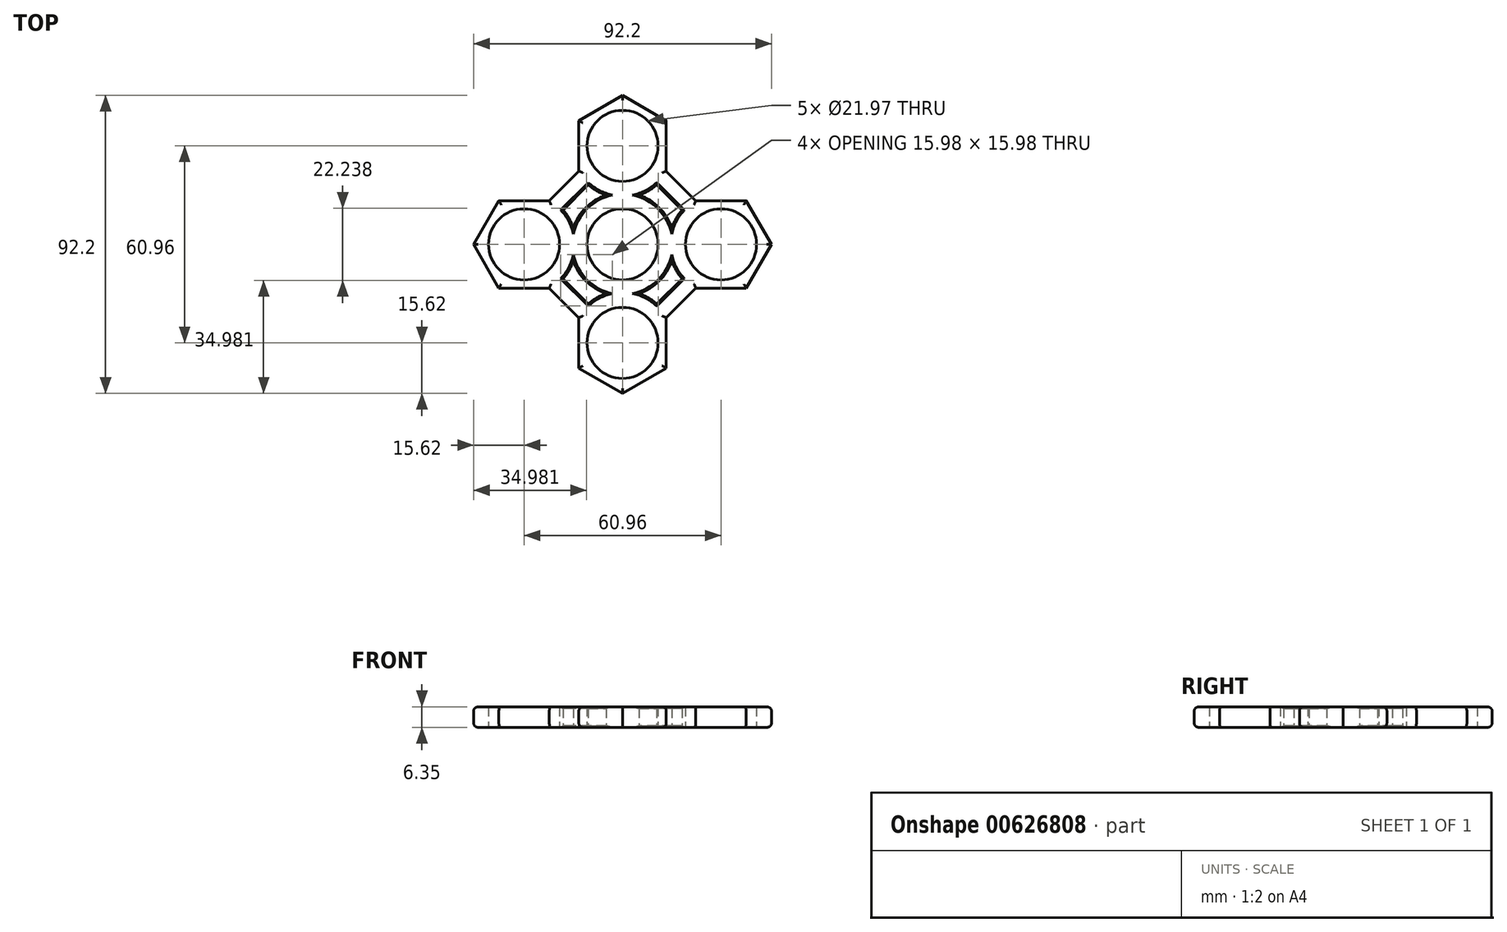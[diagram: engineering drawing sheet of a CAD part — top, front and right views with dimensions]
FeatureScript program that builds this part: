
annotation { "Feature Type Name" : "Feature", "Feature Type Description" : "" }
export const myFeature = defineFeature(function(context is Context, id is Id, definition is map)
    precondition{}
    {
        {
            var Q0;
            Q0=qCreatedBy(makeId("Top.planeOp"),FACE);
            var sketch = newSketch(context, id + "F0", { "sketchPlane" : qUnion([Q0])});
            skCircle(sketch, "E0", {"center": v(0, 0) * mm, "radius": 10.99 * mm});
            skCircle(sketch, "E1", {"center": v(0, 0) * mm, "radius": 13.53 * mm});
            skLineSegment(sketch, "E2", {"start": v(0, 0) * mm, "end": v(0, 30.48) * mm});
            skLineSegment(sketch, "E3", {"start": v(0, 0) * mm, "end": v(0, -30.48) * mm});
            skLineSegment(sketch, "E4", {"start": v(0, 0) * mm, "end": v(30.48, 0) * mm});
            skLineSegment(sketch, "E5", {"start": v(0, 0) * mm, "end": v(-30.48, 0) * mm});
            skCircle(sketch, "E6", {"center": v(0, 30.48) * mm, "radius": 13.53 * mm});
            skCircle(sketch, "E7", {"center": v(0, 30.48) * mm, "radius": 10.99 * mm});
            skCircle(sketch, "E8", {"center": v(30.48, 0) * mm, "radius": 13.53 * mm});
            skCircle(sketch, "E9", {"center": v(30.48, 0) * mm, "radius": 10.99 * mm});
            skCircle(sketch, "E10", {"center": v(0, -30.48) * mm, "radius": 13.53 * mm});
            skCircle(sketch, "E11", {"center": v(0, -30.48) * mm, "radius": 10.99 * mm});
            skCircle(sketch, "E12", {"center": v(-30.48, 0) * mm, "radius": 13.53 * mm});
            skCircle(sketch, "E13", {"center": v(-30.48, 0) * mm, "radius": 10.99 * mm});
            skCircle(sketch, "E14.cCircle", {"center": v(0, 0) * mm, "radius": 13.53 * mm, "construction": true});
            skLineSegment(sketch, "E14.0", {"start": v(13.53, 7.8) * mm, "end": v(13.53, -7.8) * mm});
            skLineSegment(sketch, "E14.1", {"start": v(13.53, -7.8) * mm, "end": v(0, -15.62) * mm});
            skLineSegment(sketch, "E14.2", {"start": v(0, -15.62) * mm, "end": v(-13.53, -7.8) * mm});
            skLineSegment(sketch, "E14.3", {"start": v(-13.53, -7.8) * mm, "end": v(-13.53, 7.8) * mm});
            skLineSegment(sketch, "E14.4", {"start": v(-13.53, 7.8) * mm, "end": v(0, 15.62) * mm});
            skLineSegment(sketch, "E14.5", {"start": v(0, 15.62) * mm, "end": v(13.53, 7.8) * mm});
            skPoint(sketch, "E14.0.midPoint", {"position": v(13.53, 0) * mm});
            skCircle(sketch, "E15.cCircle", {"center": v(0, 30.48) * mm, "radius": 13.53 * mm, "construction": true});
            skLineSegment(sketch, "E15.0", {"start": v(13.53, 38.29) * mm, "end": v(13.53, 22.67) * mm});
            skLineSegment(sketch, "E15.1", {"start": v(13.53, 22.67) * mm, "end": v(0, 14.86) * mm});
            skLineSegment(sketch, "E15.2", {"start": v(0, 14.86) * mm, "end": v(-13.53, 22.67) * mm});
            skLineSegment(sketch, "E15.3", {"start": v(-13.53, 22.67) * mm, "end": v(-13.53, 38.29) * mm});
            skLineSegment(sketch, "E15.4", {"start": v(-13.53, 38.29) * mm, "end": v(0, 46.1) * mm});
            skLineSegment(sketch, "E15.5", {"start": v(0, 46.1) * mm, "end": v(13.53, 38.29) * mm});
            skPoint(sketch, "E15.0.midPoint", {"position": v(13.53, 30.48) * mm});
            skCircle(sketch, "E16.cCircle", {"center": v(0, -30.48) * mm, "radius": 13.53 * mm, "construction": true});
            skLineSegment(sketch, "E16.0", {"start": v(13.53, -22.67) * mm, "end": v(13.53, -38.29) * mm});
            skLineSegment(sketch, "E16.1", {"start": v(13.53, -38.29) * mm, "end": v(0, -46.1) * mm});
            skLineSegment(sketch, "E16.2", {"start": v(0, -46.1) * mm, "end": v(-13.53, -38.29) * mm});
            skLineSegment(sketch, "E16.3", {"start": v(-13.53, -38.29) * mm, "end": v(-13.53, -22.67) * mm});
            skLineSegment(sketch, "E16.4", {"start": v(-13.53, -22.67) * mm, "end": v(0, -14.86) * mm});
            skLineSegment(sketch, "E16.5", {"start": v(0, -14.86) * mm, "end": v(13.53, -22.67) * mm});
            skPoint(sketch, "E16.0.midPoint", {"position": v(13.53, -30.48) * mm});
            skCircle(sketch, "E17.cCircle", {"center": v(30.48, 0) * mm, "radius": 13.53 * mm, "construction": true});
            skLineSegment(sketch, "E17.0", {"start": v(22.67, 13.53) * mm, "end": v(38.29, 13.53) * mm});
            skLineSegment(sketch, "E17.1", {"start": v(38.29, 13.53) * mm, "end": v(46.1, 0) * mm});
            skLineSegment(sketch, "E17.2", {"start": v(46.1, 0) * mm, "end": v(38.29, -13.53) * mm});
            skLineSegment(sketch, "E17.3", {"start": v(38.29, -13.53) * mm, "end": v(22.67, -13.53) * mm});
            skLineSegment(sketch, "E17.4", {"start": v(22.67, -13.53) * mm, "end": v(14.86, 0) * mm});
            skLineSegment(sketch, "E17.5", {"start": v(14.86, 0) * mm, "end": v(22.67, 13.53) * mm});
            skPoint(sketch, "E17.0.midPoint", {"position": v(30.48, 13.53) * mm});
            skCircle(sketch, "E18.cCircle", {"center": v(-30.48, 0) * mm, "radius": 13.53 * mm, "construction": true});
            skLineSegment(sketch, "E18.0", {"start": v(-22.67, -13.53) * mm, "end": v(-38.29, -13.53) * mm});
            skLineSegment(sketch, "E18.1", {"start": v(-38.29, -13.53) * mm, "end": v(-46.1, 0) * mm});
            skLineSegment(sketch, "E18.2", {"start": v(-46.1, 0) * mm, "end": v(-38.29, 13.53) * mm});
            skLineSegment(sketch, "E18.3", {"start": v(-38.29, 13.53) * mm, "end": v(-22.67, 13.53) * mm});
            skLineSegment(sketch, "E18.4", {"start": v(-22.67, 13.53) * mm, "end": v(-14.86, 0) * mm});
            skLineSegment(sketch, "E18.5", {"start": v(-14.86, 0) * mm, "end": v(-22.67, -13.53) * mm});
            skPoint(sketch, "E18.0.midPoint", {"position": v(-30.48, -13.53) * mm});
            skLineSegment(sketch, "E19", {"start": v(-22.67, 13.53) * mm, "end": v(-13.53, 22.67) * mm});
            skLineSegment(sketch, "E20", {"start": v(-22.67, -13.53) * mm, "end": v(-13.53, -22.67) * mm});
            skLineSegment(sketch, "E21", {"start": v(13.53, -22.67) * mm, "end": v(22.67, -13.53) * mm});
            skLineSegment(sketch, "E22", {"start": v(22.67, 13.53) * mm, "end": v(13.53, 22.67) * mm});
            skSolve(sketch);
        }
        {
            var Q0;
            {var subQ0=sQuery(id+"F0.wireOp",EDGE,"E14.5");var subQ3=sQuery(id+"F0.wireOp",EDGE,"E14.0");var subQ5=makeQuery(id+"F0.imprint","INTERSECT",VERTEX,{"derivedFrom":[subQ3,subQ0]});Q0=makeQuery(id+"F0.imprint","IMPRINT",FACE,{"disambiguationData":[TD([[makeQuery(id+"F0.imprint","IMPRINT",EDGE,{"disambiguationData":[TD([[subQ5,1.0]])],"derivedFrom":subQ0}),-1.0]])]});}
            var Q1;
            {var subQ0=sQuery(id+"F0.wireOp",EDGE,"E14.4");var subQ3=sQuery(id+"F0.wireOp",EDGE,"E14.3");var subQ5=makeQuery(id+"F0.imprint","INTERSECT",VERTEX,{"derivedFrom":[subQ3,subQ0]});Q1=makeQuery(id+"F0.imprint","IMPRINT",FACE,{"disambiguationData":[TD([[makeQuery(id+"F0.imprint","IMPRINT",EDGE,{"disambiguationData":[TD([[subQ5,-1.0]])],"derivedFrom":subQ0}),-1.0]])]});}
            var Q2;
            {var subQ0=sQuery(id+"F0.wireOp",EDGE,"E14.2");var subQ3=sQuery(id+"F0.wireOp",EDGE,"E14.3");var subQ5=makeQuery(id+"F0.imprint","INTERSECT",VERTEX,{"derivedFrom":[subQ0,subQ3]});Q2=makeQuery(id+"F0.imprint","IMPRINT",FACE,{"disambiguationData":[TD([[makeQuery(id+"F0.imprint","IMPRINT",EDGE,{"disambiguationData":[TD([[subQ5,1.0]])],"derivedFrom":subQ0}),-1.0]])]});}
            var Q3;
            {var subQ0=sQuery(id+"F0.wireOp",EDGE,"E14.1");var subQ3=sQuery(id+"F0.wireOp",EDGE,"E14.0");var subQ5=makeQuery(id+"F0.imprint","INTERSECT",VERTEX,{"derivedFrom":[subQ3,subQ0]});Q3=makeQuery(id+"F0.imprint","IMPRINT",FACE,{"disambiguationData":[TD([[makeQuery(id+"F0.imprint","IMPRINT",EDGE,{"disambiguationData":[TD([[subQ5,-1.0]])],"derivedFrom":subQ0}),-1.0]])]});}
            var Q4;
            {var subQ0=sQuery(id+"F0.wireOp",EDGE,"E15.5");var subQ1=sQuery(id+"F0.wireOp",EDGE,"E6");var subQ2=makeQuery(id+"F0.imprint","INTERSECT",VERTEX,{"derivedFrom":[subQ1,subQ0]});Q4=makeQuery(id+"F0.imprint","IMPRINT",FACE,{"disambiguationData":[TD([[makeQuery(id+"F0.imprint","IMPRINT",EDGE,{"disambiguationData":[TD([[subQ2,1.0]])],"derivedFrom":subQ1}),-1.0]])]});}
            var Q5;
            {var subQ0=sQuery(id+"F0.wireOp",EDGE,"E15.5");var subQ1=sQuery(id+"F0.wireOp",EDGE,"E6");var subQ2=makeQuery(id+"F0.imprint","INTERSECT",VERTEX,{"derivedFrom":[subQ1,subQ0]});Q5=makeQuery(id+"F0.imprint","IMPRINT",FACE,{"disambiguationData":[TD([[makeQuery(id+"F0.imprint","IMPRINT",EDGE,{"disambiguationData":[TD([[subQ2,-1.0]])],"derivedFrom":subQ1}),-1.0]])]});}
            var Q6;
            {var subQ0=sQuery(id+"F0.wireOp",EDGE,"E15.4");var subQ1=sQuery(id+"F0.wireOp",EDGE,"E6");var subQ2=makeQuery(id+"F0.imprint","INTERSECT",VERTEX,{"derivedFrom":[subQ1,subQ0]});Q6=makeQuery(id+"F0.imprint","IMPRINT",FACE,{"disambiguationData":[TD([[makeQuery(id+"F0.imprint","IMPRINT",EDGE,{"disambiguationData":[TD([[subQ2,-1.0]])],"derivedFrom":subQ1}),-1.0]])]});}
            var Q7;
            {var subQ0=sQuery(id+"F0.wireOp",EDGE,"E15.3");var subQ1=sQuery(id+"F0.wireOp",EDGE,"E6");var subQ2=makeQuery(id+"F0.imprint","INTERSECT",VERTEX,{"derivedFrom":[subQ1,subQ0]});Q7=makeQuery(id+"F0.imprint","IMPRINT",FACE,{"disambiguationData":[TD([[makeQuery(id+"F0.imprint","IMPRINT",EDGE,{"disambiguationData":[TD([[subQ2,-1.0]])],"derivedFrom":subQ1}),-1.0]])]});}
            var Q8;
            {var subQ0=sQuery(id+"F0.wireOp",EDGE,"E15.0");var subQ1=sQuery(id+"F0.wireOp",EDGE,"E6");var subQ2=makeQuery(id+"F0.imprint","INTERSECT",VERTEX,{"derivedFrom":[subQ1,subQ0]});Q8=makeQuery(id+"F0.imprint","IMPRINT",FACE,{"disambiguationData":[TD([[makeQuery(id+"F0.imprint","IMPRINT",EDGE,{"disambiguationData":[TD([[subQ2,1.0]])],"derivedFrom":subQ1}),-1.0]])]});}
            var Q9;
            {var subQ0=sQuery(id+"F0.wireOp",EDGE,"E17.0");var subQ1=sQuery(id+"F0.wireOp",EDGE,"E8");var subQ2=makeQuery(id+"F0.imprint","INTERSECT",VERTEX,{"derivedFrom":[subQ1,subQ0]});Q9=makeQuery(id+"F0.imprint","IMPRINT",FACE,{"disambiguationData":[TD([[makeQuery(id+"F0.imprint","IMPRINT",EDGE,{"disambiguationData":[TD([[subQ2,1.0]])],"derivedFrom":subQ1}),-1.0]])]});}
            var Q10;
            {var subQ0=sQuery(id+"F0.wireOp",EDGE,"E17.0");var subQ1=sQuery(id+"F0.wireOp",EDGE,"E8");var subQ2=makeQuery(id+"F0.imprint","INTERSECT",VERTEX,{"derivedFrom":[subQ1,subQ0]});Q10=makeQuery(id+"F0.imprint","IMPRINT",FACE,{"disambiguationData":[TD([[makeQuery(id+"F0.imprint","IMPRINT",EDGE,{"disambiguationData":[TD([[subQ2,-1.0]])],"derivedFrom":subQ1}),-1.0]])]});}
            var Q11;
            {var subQ0=sQuery(id+"F0.wireOp",EDGE,"E17.4");var subQ1=sQuery(id+"F0.wireOp",EDGE,"E8");var subQ2=makeQuery(id+"F0.imprint","INTERSECT",VERTEX,{"derivedFrom":[subQ1,subQ0]});Q11=makeQuery(id+"F0.imprint","IMPRINT",FACE,{"disambiguationData":[TD([[makeQuery(id+"F0.imprint","IMPRINT",EDGE,{"disambiguationData":[TD([[subQ2,-1.0]])],"derivedFrom":subQ1}),-1.0]])]});}
            var Q12;
            {var subQ0=sQuery(id+"F0.wireOp",EDGE,"E17.3");var subQ1=sQuery(id+"F0.wireOp",EDGE,"E8");var subQ2=makeQuery(id+"F0.imprint","INTERSECT",VERTEX,{"derivedFrom":[subQ1,subQ0]});Q12=makeQuery(id+"F0.imprint","IMPRINT",FACE,{"disambiguationData":[TD([[makeQuery(id+"F0.imprint","IMPRINT",EDGE,{"disambiguationData":[TD([[subQ2,-1.0]])],"derivedFrom":subQ1}),-1.0]])]});}
            var Q13;
            {var subQ0=sQuery(id+"F0.wireOp",EDGE,"E17.1");var subQ1=sQuery(id+"F0.wireOp",EDGE,"E8");var subQ2=makeQuery(id+"F0.imprint","INTERSECT",VERTEX,{"derivedFrom":[subQ1,subQ0]});Q13=makeQuery(id+"F0.imprint","IMPRINT",FACE,{"disambiguationData":[TD([[makeQuery(id+"F0.imprint","IMPRINT",EDGE,{"disambiguationData":[TD([[subQ2,1.0]])],"derivedFrom":subQ1}),-1.0]])]});}
            var Q14;
            {var subQ0=sQuery(id+"F0.wireOp",EDGE,"E16.5");var subQ1=sQuery(id+"F0.wireOp",EDGE,"E10");var subQ2=makeQuery(id+"F0.imprint","INTERSECT",VERTEX,{"derivedFrom":[subQ1,subQ0]});Q14=makeQuery(id+"F0.imprint","IMPRINT",FACE,{"disambiguationData":[TD([[makeQuery(id+"F0.imprint","IMPRINT",EDGE,{"disambiguationData":[TD([[subQ2,1.0]])],"derivedFrom":subQ1}),-1.0]])]});}
            var Q15;
            {var subQ0=sQuery(id+"F0.wireOp",EDGE,"E16.4");var subQ1=sQuery(id+"F0.wireOp",EDGE,"E10");var subQ2=makeQuery(id+"F0.imprint","INTERSECT",VERTEX,{"derivedFrom":[subQ1,subQ0]});Q15=makeQuery(id+"F0.imprint","IMPRINT",FACE,{"disambiguationData":[TD([[makeQuery(id+"F0.imprint","IMPRINT",EDGE,{"disambiguationData":[TD([[subQ2,-1.0]])],"derivedFrom":subQ1}),-1.0]])]});}
            var Q16;
            {var subQ0=sQuery(id+"F0.wireOp",EDGE,"E16.3");var subQ1=sQuery(id+"F0.wireOp",EDGE,"E10");var subQ2=makeQuery(id+"F0.imprint","INTERSECT",VERTEX,{"derivedFrom":[subQ1,subQ0]});Q16=makeQuery(id+"F0.imprint","IMPRINT",FACE,{"disambiguationData":[TD([[makeQuery(id+"F0.imprint","IMPRINT",EDGE,{"disambiguationData":[TD([[subQ2,-1.0]])],"derivedFrom":subQ1}),-1.0]])]});}
            var Q17;
            {var subQ0=sQuery(id+"F0.wireOp",EDGE,"E16.2");var subQ1=sQuery(id+"F0.wireOp",EDGE,"E10");var subQ2=makeQuery(id+"F0.imprint","INTERSECT",VERTEX,{"derivedFrom":[subQ1,subQ0]});Q17=makeQuery(id+"F0.imprint","IMPRINT",FACE,{"disambiguationData":[TD([[makeQuery(id+"F0.imprint","IMPRINT",EDGE,{"disambiguationData":[TD([[subQ2,-1.0]])],"derivedFrom":subQ1}),-1.0]])]});}
            var Q18;
            {var subQ0=sQuery(id+"F0.wireOp",EDGE,"E16.0");var subQ1=sQuery(id+"F0.wireOp",EDGE,"E10");var subQ2=makeQuery(id+"F0.imprint","INTERSECT",VERTEX,{"derivedFrom":[subQ1,subQ0]});Q18=makeQuery(id+"F0.imprint","IMPRINT",FACE,{"disambiguationData":[TD([[makeQuery(id+"F0.imprint","IMPRINT",EDGE,{"disambiguationData":[TD([[subQ2,1.0]])],"derivedFrom":subQ1}),-1.0]])]});}
            var Q19;
            {var subQ0=sQuery(id+"F0.wireOp",EDGE,"E18.4");var subQ1=sQuery(id+"F0.wireOp",EDGE,"E12");var subQ2=makeQuery(id+"F0.imprint","INTERSECT",VERTEX,{"derivedFrom":[subQ1,subQ0]});Q19=makeQuery(id+"F0.imprint","IMPRINT",FACE,{"disambiguationData":[TD([[makeQuery(id+"F0.imprint","IMPRINT",EDGE,{"disambiguationData":[TD([[subQ2,-1.0]])],"derivedFrom":subQ1}),-1.0]])]});}
            var Q20;
            {var subQ0=sQuery(id+"F0.wireOp",EDGE,"E18.3");var subQ1=sQuery(id+"F0.wireOp",EDGE,"E12");var subQ2=makeQuery(id+"F0.imprint","INTERSECT",VERTEX,{"derivedFrom":[subQ1,subQ0]});Q20=makeQuery(id+"F0.imprint","IMPRINT",FACE,{"disambiguationData":[TD([[makeQuery(id+"F0.imprint","IMPRINT",EDGE,{"disambiguationData":[TD([[subQ2,-1.0]])],"derivedFrom":subQ1}),-1.0]])]});}
            var Q21;
            {var subQ0=sQuery(id+"F0.wireOp",EDGE,"E18.2");var subQ1=sQuery(id+"F0.wireOp",EDGE,"E12");var subQ2=makeQuery(id+"F0.imprint","INTERSECT",VERTEX,{"derivedFrom":[subQ1,subQ0]});Q21=makeQuery(id+"F0.imprint","IMPRINT",FACE,{"disambiguationData":[TD([[makeQuery(id+"F0.imprint","IMPRINT",EDGE,{"disambiguationData":[TD([[subQ2,-1.0]])],"derivedFrom":subQ1}),-1.0]])]});}
            var Q22;
            {var subQ0=sQuery(id+"F0.wireOp",EDGE,"E18.1");var subQ1=sQuery(id+"F0.wireOp",EDGE,"E12");var subQ2=makeQuery(id+"F0.imprint","INTERSECT",VERTEX,{"derivedFrom":[subQ1,subQ0]});Q22=makeQuery(id+"F0.imprint","IMPRINT",FACE,{"disambiguationData":[TD([[makeQuery(id+"F0.imprint","IMPRINT",EDGE,{"disambiguationData":[TD([[subQ2,-1.0]])],"derivedFrom":subQ1}),-1.0]])]});}
            var Q23;
            {var subQ0=sQuery(id+"F0.wireOp",EDGE,"E18.0");var subQ1=sQuery(id+"F0.wireOp",EDGE,"E12");var subQ2=makeQuery(id+"F0.imprint","INTERSECT",VERTEX,{"derivedFrom":[subQ1,subQ0]});Q23=makeQuery(id+"F0.imprint","IMPRINT",FACE,{"disambiguationData":[TD([[makeQuery(id+"F0.imprint","IMPRINT",EDGE,{"disambiguationData":[TD([[subQ2,-1.0]])],"derivedFrom":subQ1}),-1.0]])]});}
            var Q24;
            {var subQ1=sQuery(id+"F0.wireOp",EDGE,"E4");var subQ3=sQuery(id+"F0.wireOp",EDGE,"E8");var subQ4=makeQuery(id+"F0.imprint","INTERSECT",VERTEX,{"derivedFrom":[subQ1,subQ3]});Q24=makeQuery(id+"F0.imprint","IMPRINT",FACE,{"disambiguationData":[TD([[makeQuery(id+"F0.imprint","IMPRINT",EDGE,{"disambiguationData":[TD([[subQ4,1.0]])],"derivedFrom":subQ3}),-1.0]])]});}
            var Q25;
            {var subQ1=sQuery(id+"F0.wireOp",EDGE,"E4");var subQ3=sQuery(id+"F0.wireOp",EDGE,"E8");var subQ4=makeQuery(id+"F0.imprint","INTERSECT",VERTEX,{"derivedFrom":[subQ1,subQ3]});Q25=makeQuery(id+"F0.imprint","IMPRINT",FACE,{"disambiguationData":[TD([[makeQuery(id+"F0.imprint","IMPRINT",EDGE,{"disambiguationData":[TD([[subQ4,-1.0]])],"derivedFrom":subQ3}),-1.0]])]});}
            var Q26;
            {var subQ1=sQuery(id+"F0.wireOp",EDGE,"E5");var subQ3=sQuery(id+"F0.wireOp",EDGE,"E12");var subQ4=makeQuery(id+"F0.imprint","INTERSECT",VERTEX,{"derivedFrom":[subQ1,subQ3]});Q26=makeQuery(id+"F0.imprint","IMPRINT",FACE,{"disambiguationData":[TD([[makeQuery(id+"F0.imprint","IMPRINT",EDGE,{"disambiguationData":[TD([[subQ4,-1.0]])],"derivedFrom":subQ3}),-1.0]])]});}
            var Q27;
            {var subQ1=sQuery(id+"F0.wireOp",EDGE,"E5");var subQ3=sQuery(id+"F0.wireOp",EDGE,"E12");var subQ4=makeQuery(id+"F0.imprint","INTERSECT",VERTEX,{"derivedFrom":[subQ1,subQ3]});Q27=makeQuery(id+"F0.imprint","IMPRINT",FACE,{"disambiguationData":[TD([[makeQuery(id+"F0.imprint","IMPRINT",EDGE,{"disambiguationData":[TD([[subQ4,1.0]])],"derivedFrom":subQ3}),-1.0]])]});}
            var Q28;
            {var subQ0=sQuery(id+"F0.wireOp",EDGE,"E14.5");var subQ1=sQuery(id+"F0.wireOp",EDGE,"E1");var subQ2=makeQuery(id+"F0.imprint","INTERSECT",VERTEX,{"derivedFrom":[subQ1,subQ0]});Q28=makeQuery(id+"F0.imprint","IMPRINT",FACE,{"disambiguationData":[TD([[makeQuery(id+"F0.imprint","IMPRINT",EDGE,{"disambiguationData":[TD([[subQ2,-1.0]])],"derivedFrom":subQ1}),-1.0]])]});}
            var Q29;
            {var subQ0=sQuery(id+"F0.wireOp",EDGE,"E14.4");var subQ1=sQuery(id+"F0.wireOp",EDGE,"E1");var subQ2=makeQuery(id+"F0.imprint","INTERSECT",VERTEX,{"derivedFrom":[subQ1,subQ0]});Q29=makeQuery(id+"F0.imprint","IMPRINT",FACE,{"disambiguationData":[TD([[makeQuery(id+"F0.imprint","IMPRINT",EDGE,{"disambiguationData":[TD([[subQ2,1.0]])],"derivedFrom":subQ1}),-1.0]])]});}
            var Q30;
            {var subQ0=sQuery(id+"F0.wireOp",EDGE,"E14.2");var subQ1=sQuery(id+"F0.wireOp",EDGE,"E1");var subQ2=makeQuery(id+"F0.imprint","INTERSECT",VERTEX,{"derivedFrom":[subQ1,subQ0]});Q30=makeQuery(id+"F0.imprint","IMPRINT",FACE,{"disambiguationData":[TD([[makeQuery(id+"F0.imprint","IMPRINT",EDGE,{"disambiguationData":[TD([[subQ2,-1.0]])],"derivedFrom":subQ1}),-1.0]])]});}
            var Q31;
            {var subQ0=sQuery(id+"F0.wireOp",EDGE,"E14.1");var subQ1=sQuery(id+"F0.wireOp",EDGE,"E1");var subQ2=makeQuery(id+"F0.imprint","INTERSECT",VERTEX,{"derivedFrom":[subQ1,subQ0]});Q31=makeQuery(id+"F0.imprint","IMPRINT",FACE,{"disambiguationData":[TD([[makeQuery(id+"F0.imprint","IMPRINT",EDGE,{"disambiguationData":[TD([[subQ2,1.0]])],"derivedFrom":subQ1}),-1.0]])]});}
            var Q32;
            {var subQ0=sQuery(id+"F0.wireOp",EDGE,"E14.4");var subQ3=sQuery(id+"F0.wireOp",EDGE,"E15.2");var subQ5=makeQuery(id+"F0.imprint","INTERSECT",VERTEX,{"derivedFrom":[subQ0,subQ3]});Q32=makeQuery(id+"F0.imprint","IMPRINT",FACE,{"disambiguationData":[TD([[makeQuery(id+"F0.imprint","IMPRINT",EDGE,{"disambiguationData":[TD([[subQ5,-1.0]])],"derivedFrom":subQ0}),-1.0]])]});}
            var Q33;
            {var subQ0=sQuery(id+"F0.wireOp",EDGE,"E14.5");var subQ3=sQuery(id+"F0.wireOp",EDGE,"E15.1");var subQ5=makeQuery(id+"F0.imprint","INTERSECT",VERTEX,{"derivedFrom":[subQ0,subQ3]});Q33=makeQuery(id+"F0.imprint","IMPRINT",FACE,{"disambiguationData":[TD([[makeQuery(id+"F0.imprint","IMPRINT",EDGE,{"disambiguationData":[TD([[subQ5,1.0]])],"derivedFrom":subQ0}),-1.0]])]});}
            var Q34;
            {var subQ1=sQuery(id+"F0.wireOp",EDGE,"E2");var subQ3=sQuery(id+"F0.wireOp",EDGE,"E6");var subQ4=makeQuery(id+"F0.imprint","INTERSECT",VERTEX,{"derivedFrom":[subQ1,subQ3]});Q34=makeQuery(id+"F0.imprint","IMPRINT",FACE,{"disambiguationData":[TD([[makeQuery(id+"F0.imprint","IMPRINT",EDGE,{"disambiguationData":[TD([[subQ4,1.0]])],"derivedFrom":subQ3}),-1.0]])]});}
            var Q35;
            {var subQ1=sQuery(id+"F0.wireOp",EDGE,"E2");var subQ3=sQuery(id+"F0.wireOp",EDGE,"E6");var subQ4=makeQuery(id+"F0.imprint","INTERSECT",VERTEX,{"derivedFrom":[subQ1,subQ3]});Q35=makeQuery(id+"F0.imprint","IMPRINT",FACE,{"disambiguationData":[TD([[makeQuery(id+"F0.imprint","IMPRINT",EDGE,{"disambiguationData":[TD([[subQ4,-1.0]])],"derivedFrom":subQ3}),-1.0]])]});}
            var Q36;
            {var subQ0=sQuery(id+"F0.wireOp",EDGE,"E14.1");var subQ3=sQuery(id+"F0.wireOp",EDGE,"E16.5");var subQ5=makeQuery(id+"F0.imprint","INTERSECT",VERTEX,{"derivedFrom":[subQ0,subQ3]});Q36=makeQuery(id+"F0.imprint","IMPRINT",FACE,{"disambiguationData":[TD([[makeQuery(id+"F0.imprint","IMPRINT",EDGE,{"disambiguationData":[TD([[subQ5,-1.0]])],"derivedFrom":subQ0}),-1.0]])]});}
            var Q37;
            {var subQ0=sQuery(id+"F0.wireOp",EDGE,"E14.2");var subQ3=sQuery(id+"F0.wireOp",EDGE,"E16.4");var subQ5=makeQuery(id+"F0.imprint","INTERSECT",VERTEX,{"derivedFrom":[subQ0,subQ3]});Q37=makeQuery(id+"F0.imprint","IMPRINT",FACE,{"disambiguationData":[TD([[makeQuery(id+"F0.imprint","IMPRINT",EDGE,{"disambiguationData":[TD([[subQ5,1.0]])],"derivedFrom":subQ0}),-1.0]])]});}
            var Q38;
            {var subQ1=sQuery(id+"F0.wireOp",EDGE,"E3");var subQ3=sQuery(id+"F0.wireOp",EDGE,"E10");var subQ4=makeQuery(id+"F0.imprint","INTERSECT",VERTEX,{"derivedFrom":[subQ1,subQ3]});Q38=makeQuery(id+"F0.imprint","IMPRINT",FACE,{"disambiguationData":[TD([[makeQuery(id+"F0.imprint","IMPRINT",EDGE,{"disambiguationData":[TD([[subQ4,1.0]])],"derivedFrom":subQ3}),-1.0]])]});}
            var Q39;
            {var subQ1=sQuery(id+"F0.wireOp",EDGE,"E3");var subQ3=sQuery(id+"F0.wireOp",EDGE,"E10");var subQ4=makeQuery(id+"F0.imprint","INTERSECT",VERTEX,{"derivedFrom":[subQ1,subQ3]});Q39=makeQuery(id+"F0.imprint","IMPRINT",FACE,{"disambiguationData":[TD([[makeQuery(id+"F0.imprint","IMPRINT",EDGE,{"disambiguationData":[TD([[subQ4,-1.0]])],"derivedFrom":subQ3}),-1.0]])]});}
            var Q40;
            {var subQ0=sQuery(id+"F0.wireOp",EDGE,"E2");var subQ1=sQuery(id+"F0.wireOp",EDGE,"E0");var subQ2=makeQuery(id+"F0.imprint","INTERSECT",VERTEX,{"derivedFrom":[subQ1,subQ0]});Q40=makeQuery(id+"F0.imprint","IMPRINT",FACE,{"disambiguationData":[TD([[makeQuery(id+"F0.imprint","IMPRINT",EDGE,{"disambiguationData":[TD([[subQ2,1.0]])],"derivedFrom":subQ1}),-1.0]])]});}
            var Q41;
            {var subQ0=sQuery(id+"F0.wireOp",EDGE,"E2");var subQ1=sQuery(id+"F0.wireOp",EDGE,"E0");var subQ2=makeQuery(id+"F0.imprint","INTERSECT",VERTEX,{"derivedFrom":[subQ1,subQ0]});Q41=makeQuery(id+"F0.imprint","IMPRINT",FACE,{"disambiguationData":[TD([[makeQuery(id+"F0.imprint","IMPRINT",EDGE,{"disambiguationData":[TD([[subQ2,-1.0]])],"derivedFrom":subQ1}),-1.0]])]});}
            var Q42;
            {var subQ4=sQuery(id+"F0.wireOp",EDGE,"E0");var subQ6=sQuery(id+"F0.wireOp",EDGE,"E5");var subQ8=makeQuery(id+"F0.imprint","INTERSECT",VERTEX,{"derivedFrom":[subQ4,subQ6]});Q42=makeQuery(id+"F0.imprint","IMPRINT",FACE,{"disambiguationData":[TD([[makeQuery(id+"F0.imprint","IMPRINT",EDGE,{"disambiguationData":[TD([[subQ8,-1.0]])],"derivedFrom":subQ4}),-1.0]])]});}
            var Q43;
            {var subQ2=sQuery(id+"F0.wireOp",EDGE,"E4");var subQ6=sQuery(id+"F0.wireOp",EDGE,"E0");var subQ8=makeQuery(id+"F0.imprint","INTERSECT",VERTEX,{"derivedFrom":[subQ6,subQ2]});Q43=makeQuery(id+"F0.imprint","IMPRINT",FACE,{"disambiguationData":[TD([[makeQuery(id+"F0.imprint","IMPRINT",EDGE,{"disambiguationData":[TD([[subQ8,1.0]])],"derivedFrom":subQ6}),-1.0]])]});}
            var Q44;
            Q44=makeQuery(id+"F0.imprint","IMPRINT",FACE,{"disambiguationData":[TD([[makeQuery(id+"F0.imprint","IMPRINT",EDGE,{"derivedFrom":sQuery(id+"F0.wireOp",EDGE,"E7")}),-1.0]])]});
            var Q45;
            Q45=makeQuery(id+"F0.imprint","IMPRINT",FACE,{"disambiguationData":[TD([[makeQuery(id+"F0.imprint","IMPRINT",EDGE,{"derivedFrom":sQuery(id+"F0.wireOp",EDGE,"E9")}),-1.0]])]});
            var Q46;
            Q46=makeQuery(id+"F0.imprint","IMPRINT",FACE,{"disambiguationData":[TD([[makeQuery(id+"F0.imprint","IMPRINT",EDGE,{"derivedFrom":sQuery(id+"F0.wireOp",EDGE,"E11")}),-1.0]])]});
            var Q47;
            Q47=makeQuery(id+"F0.imprint","IMPRINT",FACE,{"disambiguationData":[TD([[makeQuery(id+"F0.imprint","IMPRINT",EDGE,{"derivedFrom":sQuery(id+"F0.wireOp",EDGE,"E13")}),-1.0]])]});
            var Q48;
            {var subQ10=sQuery(id+"F0.wireOp",EDGE,"E19");Q48=makeQuery(id+"F0.imprint","IMPRINT",FACE,{"disambiguationData":[TD([[makeQuery(id+"F0.imprint","IMPRINT",EDGE,{"derivedFrom":subQ10}),-1.0]])]});}
            var Q49;
            {var subQ9=sQuery(id+"F0.wireOp",EDGE,"E22");Q49=makeQuery(id+"F0.imprint","IMPRINT",FACE,{"disambiguationData":[TD([[makeQuery(id+"F0.imprint","IMPRINT",EDGE,{"derivedFrom":subQ9}),1.0]])]});}
            var Q50;
            {var subQ13=sQuery(id+"F0.wireOp",EDGE,"E21");Q50=makeQuery(id+"F0.imprint","IMPRINT",FACE,{"disambiguationData":[TD([[makeQuery(id+"F0.imprint","IMPRINT",EDGE,{"derivedFrom":subQ13}),1.0]])]});}
            var Q51;
            {var subQ12=sQuery(id+"F0.wireOp",EDGE,"E20");Q51=makeQuery(id+"F0.imprint","IMPRINT",FACE,{"disambiguationData":[TD([[makeQuery(id+"F0.imprint","IMPRINT",EDGE,{"derivedFrom":subQ12}),1.0]])]});}
            extrude(context, id + "F1", {"entities" : qUnion([Q0, Q1, Q2, Q3, Q4, Q5, Q6, Q7, Q8, Q9, Q10, Q11, Q12, Q13, Q14, Q15, Q16, Q17, Q18, Q19, Q20, Q21, Q22, Q23, Q24, Q25, Q26, Q27, Q28, Q29, Q30, Q31, Q32, Q33, Q34, Q35, Q36, Q37, Q38, Q39, Q40, Q41, Q42, Q43, Q44, Q45, Q46, Q47, Q48, Q49, Q50, Q51]), "depth" : 6.35 * mm, "offsetDistance" : 25.4 * mm});
        }
        {
            var Q0;
            Q0=makeQuery(id+"F3.opFillet","SPLIT",FACE,{"disambiguationData":[OD(12.0)],"derivedFrom":makeQuery(id+"F1.opExtrude","CAP_FACE",FACE,{"disambiguationData":[OSD([sQuery(id+"F0.wireOp",EDGE,"E0"),sQuery(id+"F0.wireOp",EDGE,"E7"),sQuery(id+"F0.wireOp",EDGE,"E9"),sQuery(id+"F0.wireOp",EDGE,"E11"),sQuery(id+"F0.wireOp",EDGE,"E13"),sQuery(id+"F0.wireOp",EDGE,"E15.0"),sQuery(id+"F0.wireOp",EDGE,"E15.3"),sQuery(id+"F0.wireOp",EDGE,"E15.4"),sQuery(id+"F0.wireOp",EDGE,"E15.5"),sQuery(id+"F0.wireOp",EDGE,"E16.0"),sQuery(id+"F0.wireOp",EDGE,"E16.1"),sQuery(id+"F0.wireOp",EDGE,"E16.2"),sQuery(id+"F0.wireOp",EDGE,"E16.3"),sQuery(id+"F0.wireOp",EDGE,"E17.0"),sQuery(id+"F0.wireOp",EDGE,"E17.1"),sQuery(id+"F0.wireOp",EDGE,"E17.2"),sQuery(id+"F0.wireOp",EDGE,"E17.3"),sQuery(id+"F0.wireOp",EDGE,"E18.0"),sQuery(id+"F0.wireOp",EDGE,"E18.1"),sQuery(id+"F0.wireOp",EDGE,"E18.2"),sQuery(id+"F0.wireOp",EDGE,"E18.3"),sQuery(id+"F0.wireOp",EDGE,"E19"),sQuery(id+"F0.wireOp",EDGE,"E20"),sQuery(id+"F0.wireOp",EDGE,"E21"),sQuery(id+"F0.wireOp",EDGE,"E22")])],"isStart":false})});
            var Q1;
            Q1=makeQuery(id+"F1.opExtrude","CAP_FACE",FACE,{"disambiguationData":[OSD([sQuery(id+"F0.wireOp",EDGE,"E0"),sQuery(id+"F0.wireOp",EDGE,"E7"),sQuery(id+"F0.wireOp",EDGE,"E9"),sQuery(id+"F0.wireOp",EDGE,"E11"),sQuery(id+"F0.wireOp",EDGE,"E13"),sQuery(id+"F0.wireOp",EDGE,"E15.0"),sQuery(id+"F0.wireOp",EDGE,"E15.3"),sQuery(id+"F0.wireOp",EDGE,"E15.4"),sQuery(id+"F0.wireOp",EDGE,"E15.5"),sQuery(id+"F0.wireOp",EDGE,"E16.0"),sQuery(id+"F0.wireOp",EDGE,"E16.1"),sQuery(id+"F0.wireOp",EDGE,"E16.2"),sQuery(id+"F0.wireOp",EDGE,"E16.3"),sQuery(id+"F0.wireOp",EDGE,"E17.0"),sQuery(id+"F0.wireOp",EDGE,"E17.1"),sQuery(id+"F0.wireOp",EDGE,"E17.2"),sQuery(id+"F0.wireOp",EDGE,"E17.3"),sQuery(id+"F0.wireOp",EDGE,"E18.0"),sQuery(id+"F0.wireOp",EDGE,"E18.1"),sQuery(id+"F0.wireOp",EDGE,"E18.2"),sQuery(id+"F0.wireOp",EDGE,"E18.3"),sQuery(id+"F0.wireOp",EDGE,"E19"),sQuery(id+"F0.wireOp",EDGE,"E20"),sQuery(id+"F0.wireOp",EDGE,"E21"),sQuery(id+"F0.wireOp",EDGE,"E22")])],"isStart":true});
            shell(context, id + "F2", {"entities" : qUnion([Q0, Q1]), "thickness" : 5.08 * mm});
        }
        {
            var Q0;
            Q0=makeQuery(id+"F1.opExtrude","CAP_EDGE",EDGE,{"disambiguationData":[OSD([sQuery(id+"F0.wireOp",EDGE,"E18.1")])],"isStart":false});
            var Q1;
            Q1=makeQuery(id+"F1.opExtrude","CAP_EDGE",EDGE,{"disambiguationData":[OSD([sQuery(id+"F0.wireOp",EDGE,"E18.2")])],"isStart":false});
            var Q2;
            Q2=makeQuery(id+"F1.opExtrude","CAP_EDGE",EDGE,{"disambiguationData":[OSD([sQuery(id+"F0.wireOp",EDGE,"E18.3")])],"isStart":false});
            var Q3;
            Q3=makeQuery(id+"F1.opExtrude","CAP_EDGE",EDGE,{"disambiguationData":[OSD([sQuery(id+"F0.wireOp",EDGE,"E19")])],"isStart":false});
            var Q4;
            Q4=makeQuery(id+"F1.opExtrude","CAP_EDGE",EDGE,{"disambiguationData":[OSD([sQuery(id+"F0.wireOp",EDGE,"E15.3")])],"isStart":false});
            var Q5;
            Q5=makeQuery(id+"F1.opExtrude","CAP_EDGE",EDGE,{"disambiguationData":[OSD([sQuery(id+"F0.wireOp",EDGE,"E15.4")])],"isStart":false});
            var Q6;
            Q6=makeQuery(id+"F1.opExtrude","CAP_EDGE",EDGE,{"disambiguationData":[OSD([sQuery(id+"F0.wireOp",EDGE,"E15.5")])],"isStart":false});
            var Q7;
            Q7=makeQuery(id+"F1.opExtrude","CAP_EDGE",EDGE,{"disambiguationData":[OSD([sQuery(id+"F0.wireOp",EDGE,"E15.0")])],"isStart":false});
            var Q8;
            Q8=makeQuery(id+"F1.opExtrude","CAP_EDGE",EDGE,{"disambiguationData":[OSD([sQuery(id+"F0.wireOp",EDGE,"E22")])],"isStart":false});
            var Q9;
            Q9=makeQuery(id+"F1.opExtrude","CAP_EDGE",EDGE,{"disambiguationData":[OSD([sQuery(id+"F0.wireOp",EDGE,"E17.0")])],"isStart":false});
            var Q10;
            Q10=makeQuery(id+"F1.opExtrude","CAP_EDGE",EDGE,{"disambiguationData":[OSD([sQuery(id+"F0.wireOp",EDGE,"E17.1")])],"isStart":false});
            var Q11;
            Q11=makeQuery(id+"F1.opExtrude","CAP_EDGE",EDGE,{"disambiguationData":[OSD([sQuery(id+"F0.wireOp",EDGE,"E17.2")])],"isStart":false});
            var Q12;
            Q12=makeQuery(id+"F1.opExtrude","CAP_EDGE",EDGE,{"disambiguationData":[OSD([sQuery(id+"F0.wireOp",EDGE,"E17.3")])],"isStart":false});
            var Q13;
            Q13=makeQuery(id+"F1.opExtrude","CAP_EDGE",EDGE,{"disambiguationData":[OSD([sQuery(id+"F0.wireOp",EDGE,"E21")])],"isStart":false});
            var Q14;
            Q14=makeQuery(id+"F1.opExtrude","CAP_EDGE",EDGE,{"disambiguationData":[OSD([sQuery(id+"F0.wireOp",EDGE,"E16.0")])],"isStart":false});
            var Q15;
            Q15=makeQuery(id+"F1.opExtrude","CAP_EDGE",EDGE,{"disambiguationData":[OSD([sQuery(id+"F0.wireOp",EDGE,"E16.1")])],"isStart":false});
            var Q16;
            Q16=makeQuery(id+"F1.opExtrude","CAP_EDGE",EDGE,{"disambiguationData":[OSD([sQuery(id+"F0.wireOp",EDGE,"E16.3")])],"isStart":false});
            var Q17;
            Q17=makeQuery(id+"F1.opExtrude","CAP_EDGE",EDGE,{"disambiguationData":[OSD([sQuery(id+"F0.wireOp",EDGE,"E16.2")])],"isStart":false});
            var Q18;
            Q18=makeQuery(id+"F1.opExtrude","CAP_EDGE",EDGE,{"disambiguationData":[OSD([sQuery(id+"F0.wireOp",EDGE,"E20")])],"isStart":false});
            var Q19;
            Q19=makeQuery(id+"F1.opExtrude","CAP_EDGE",EDGE,{"disambiguationData":[OSD([sQuery(id+"F0.wireOp",EDGE,"E18.0")])],"isStart":false});
            var Q20;
            Q20=makeQuery(id+"F1.opExtrude","CAP_EDGE",EDGE,{"disambiguationData":[OSD([sQuery(id+"F0.wireOp",EDGE,"E17.1")])],"isStart":true});
            var Q21;
            Q21=makeQuery(id+"F1.opExtrude","CAP_EDGE",EDGE,{"disambiguationData":[OSD([sQuery(id+"F0.wireOp",EDGE,"E17.2")])],"isStart":true});
            var Q22;
            Q22=makeQuery(id+"F1.opExtrude","CAP_EDGE",EDGE,{"disambiguationData":[OSD([sQuery(id+"F0.wireOp",EDGE,"E17.3")])],"isStart":true});
            var Q23;
            Q23=makeQuery(id+"F1.opExtrude","CAP_EDGE",EDGE,{"disambiguationData":[OSD([sQuery(id+"F0.wireOp",EDGE,"E16.0")])],"isStart":true});
            var Q24;
            Q24=makeQuery(id+"F1.opExtrude","CAP_EDGE",EDGE,{"disambiguationData":[OSD([sQuery(id+"F0.wireOp",EDGE,"E16.1")])],"isStart":true});
            var Q25;
            Q25=makeQuery(id+"F1.opExtrude","CAP_EDGE",EDGE,{"disambiguationData":[OSD([sQuery(id+"F0.wireOp",EDGE,"E16.2")])],"isStart":true});
            var Q26;
            Q26=makeQuery(id+"F1.opExtrude","CAP_EDGE",EDGE,{"disambiguationData":[OSD([sQuery(id+"F0.wireOp",EDGE,"E16.3")])],"isStart":true});
            var Q27;
            Q27=makeQuery(id+"F1.opExtrude","CAP_EDGE",EDGE,{"disambiguationData":[OSD([sQuery(id+"F0.wireOp",EDGE,"E20")])],"isStart":true});
            var Q28;
            Q28=makeQuery(id+"F1.opExtrude","CAP_EDGE",EDGE,{"disambiguationData":[OSD([sQuery(id+"F0.wireOp",EDGE,"E18.0")])],"isStart":true});
            var Q29;
            Q29=makeQuery(id+"F1.opExtrude","CAP_EDGE",EDGE,{"disambiguationData":[OSD([sQuery(id+"F0.wireOp",EDGE,"E18.1")])],"isStart":true});
            var Q30;
            Q30=makeQuery(id+"F1.opExtrude","CAP_EDGE",EDGE,{"disambiguationData":[OSD([sQuery(id+"F0.wireOp",EDGE,"E18.2")])],"isStart":true});
            var Q31;
            Q31=makeQuery(id+"F1.opExtrude","CAP_EDGE",EDGE,{"disambiguationData":[OSD([sQuery(id+"F0.wireOp",EDGE,"E19")])],"isStart":true});
            var Q32;
            Q32=makeQuery(id+"F1.opExtrude","CAP_EDGE",EDGE,{"disambiguationData":[OSD([sQuery(id+"F0.wireOp",EDGE,"E18.3")])],"isStart":true});
            var Q33;
            Q33=makeQuery(id+"F1.opExtrude","CAP_EDGE",EDGE,{"disambiguationData":[OSD([sQuery(id+"F0.wireOp",EDGE,"E15.3")])],"isStart":true});
            var Q34;
            Q34=makeQuery(id+"F1.opExtrude","CAP_EDGE",EDGE,{"disambiguationData":[OSD([sQuery(id+"F0.wireOp",EDGE,"E15.4")])],"isStart":true});
            var Q35;
            Q35=makeQuery(id+"F1.opExtrude","CAP_EDGE",EDGE,{"disambiguationData":[OSD([sQuery(id+"F0.wireOp",EDGE,"E15.5")])],"isStart":true});
            var Q36;
            Q36=makeQuery(id+"F1.opExtrude","CAP_EDGE",EDGE,{"disambiguationData":[OSD([sQuery(id+"F0.wireOp",EDGE,"E15.0")])],"isStart":true});
            var Q37;
            Q37=makeQuery(id+"F1.opExtrude","CAP_EDGE",EDGE,{"disambiguationData":[OSD([sQuery(id+"F0.wireOp",EDGE,"E22")])],"isStart":true});
            var Q38;
            Q38=makeQuery(id+"F1.opExtrude","CAP_EDGE",EDGE,{"disambiguationData":[OSD([sQuery(id+"F0.wireOp",EDGE,"E17.0")])],"isStart":true});
            var Q39;
            Q39=makeQuery(id+"F1.opExtrude","CAP_EDGE",EDGE,{"disambiguationData":[OSD([sQuery(id+"F0.wireOp",EDGE,"E21")])],"isStart":true});
            fillet(context, id + "F3", {"entities" : qUnion([Q0, Q1, Q2, Q3, Q4, Q5, Q6, Q7, Q8, Q9, Q10, Q11, Q12, Q13, Q14, Q15, Q16, Q17, Q18, Q19, Q20, Q21, Q22, Q23, Q24, Q25, Q26, Q27, Q28, Q29, Q30, Q31, Q32, Q33, Q34, Q35, Q36, Q37, Q38, Q39]), "radius" : 1.27 * mm, "tangentPropagation" : true, "allowEdgeOverflow" : false});
        }
        {
            var Q0;
            {var subQ0=sQuery(id+"F0.wireOp",EDGE,"E22");Q0=makeQuery(id+"F2.opShell","OFFSET_EDGE",EDGE,{"disambiguationData":[OSD([subQ0]),TDD([makeQuery(id+"F1.opExtrude","CAP_EDGE",EDGE,{"disambiguationData":[OSD([subQ0])],"isStart":false})])]});}
            var Q1;
            {var subQ0=sQuery(id+"F0.wireOp",EDGE,"E9");Q1=makeQuery(id+"F2.opShell","OFFSET_EDGE",EDGE,{"disambiguationData":[OSD([subQ0]),TDD([makeQuery(id+"F1.opExtrude","CAP_EDGE",EDGE,{"disambiguationData":[OSD([subQ0])],"isStart":false})]),OD(1.0)]});}
            var Q2;
            {var subQ0=sQuery(id+"F0.wireOp",EDGE,"E0");Q2=makeQuery(id+"F2.opShell","OFFSET_EDGE",EDGE,{"disambiguationData":[OSD([subQ0]),TDD([makeQuery(id+"F1.opExtrude","CAP_EDGE",EDGE,{"disambiguationData":[OSD([subQ0])],"isStart":false})]),OD(1.0)]});}
            var Q3;
            {var subQ0=sQuery(id+"F0.wireOp",EDGE,"E0");Q3=makeQuery(id+"F2.opShell","OFFSET_EDGE",EDGE,{"disambiguationData":[OSD([subQ0]),TDD([makeQuery(id+"F1.opExtrude","CAP_EDGE",EDGE,{"disambiguationData":[OSD([subQ0])],"isStart":true})]),OD(1.0)]});}
            var Q4;
            {var subQ0=sQuery(id+"F0.wireOp",EDGE,"E21");Q4=makeQuery(id+"F2.opShell","OFFSET_EDGE",EDGE,{"disambiguationData":[OSD([subQ0]),TDD([makeQuery(id+"F1.opExtrude","CAP_EDGE",EDGE,{"disambiguationData":[OSD([subQ0])],"isStart":false})])]});}
            var Q5;
            {var subQ0=sQuery(id+"F0.wireOp",EDGE,"E9");Q5=makeQuery(id+"F2.opShell","OFFSET_EDGE",EDGE,{"disambiguationData":[OSD([subQ0]),TDD([makeQuery(id+"F1.opExtrude","CAP_EDGE",EDGE,{"disambiguationData":[OSD([subQ0])],"isStart":false})]),OD(0.0)]});}
            var Q6;
            {var subQ0=sQuery(id+"F0.wireOp",EDGE,"E0");Q6=makeQuery(id+"F2.opShell","OFFSET_EDGE",EDGE,{"disambiguationData":[OSD([subQ0]),TDD([makeQuery(id+"F1.opExtrude","CAP_EDGE",EDGE,{"disambiguationData":[OSD([subQ0])],"isStart":false})]),OD(2.0)]});}
            var Q7;
            {var subQ0=sQuery(id+"F0.wireOp",EDGE,"E11");Q7=makeQuery(id+"F2.opShell","OFFSET_EDGE",EDGE,{"disambiguationData":[OSD([subQ0]),TDD([makeQuery(id+"F1.opExtrude","CAP_EDGE",EDGE,{"disambiguationData":[OSD([subQ0])],"isStart":false})]),OD(1.0)]});}
            var Q8;
            {var subQ0=sQuery(id+"F0.wireOp",EDGE,"E11");Q8=makeQuery(id+"F2.opShell","OFFSET_EDGE",EDGE,{"disambiguationData":[OSD([subQ0]),TDD([makeQuery(id+"F1.opExtrude","CAP_EDGE",EDGE,{"disambiguationData":[OSD([subQ0])],"isStart":false})]),OD(0.0)]});}
            var Q9;
            {var subQ0=sQuery(id+"F0.wireOp",EDGE,"E0");Q9=makeQuery(id+"F2.opShell","OFFSET_EDGE",EDGE,{"disambiguationData":[OSD([subQ0]),TDD([makeQuery(id+"F1.opExtrude","CAP_EDGE",EDGE,{"disambiguationData":[OSD([subQ0])],"isStart":false})]),OD(3.0)]});}
            var Q10;
            {var subQ0=sQuery(id+"F0.wireOp",EDGE,"E20");Q10=makeQuery(id+"F2.opShell","OFFSET_EDGE",EDGE,{"disambiguationData":[OSD([subQ0]),TDD([makeQuery(id+"F1.opExtrude","CAP_EDGE",EDGE,{"disambiguationData":[OSD([subQ0])],"isStart":false})])]});}
            var Q11;
            {var subQ0=sQuery(id+"F0.wireOp",EDGE,"E0");Q11=makeQuery(id+"F2.opShell","OFFSET_EDGE",EDGE,{"disambiguationData":[OSD([subQ0]),TDD([makeQuery(id+"F1.opExtrude","CAP_EDGE",EDGE,{"disambiguationData":[OSD([subQ0])],"isStart":true})]),OD(0.0)]});}
            var Q12;
            {var subQ0=sQuery(id+"F0.wireOp",EDGE,"E0");Q12=makeQuery(id+"F2.opShell","OFFSET_EDGE",EDGE,{"disambiguationData":[OSD([subQ0]),TDD([makeQuery(id+"F1.opExtrude","CAP_EDGE",EDGE,{"disambiguationData":[OSD([subQ0])],"isStart":false})]),OD(0.0)]});}
            var Q13;
            {var subQ0=sQuery(id+"F0.wireOp",EDGE,"E7");Q13=makeQuery(id+"F2.opShell","OFFSET_EDGE",EDGE,{"disambiguationData":[OSD([subQ0]),TDD([makeQuery(id+"F1.opExtrude","CAP_EDGE",EDGE,{"disambiguationData":[OSD([subQ0])],"isStart":false})]),OD(0.0)]});}
            var Q14;
            {var subQ0=sQuery(id+"F0.wireOp",EDGE,"E19");Q14=makeQuery(id+"F2.opShell","OFFSET_EDGE",EDGE,{"disambiguationData":[OSD([subQ0]),TDD([makeQuery(id+"F1.opExtrude","CAP_EDGE",EDGE,{"disambiguationData":[OSD([subQ0])],"isStart":false})])]});}
            var Q15;
            {var subQ0=sQuery(id+"F0.wireOp",EDGE,"E13");Q15=makeQuery(id+"F2.opShell","OFFSET_EDGE",EDGE,{"disambiguationData":[OSD([subQ0]),TDD([makeQuery(id+"F1.opExtrude","CAP_EDGE",EDGE,{"disambiguationData":[OSD([subQ0])],"isStart":false})]),OD(0.0)]});}
            var Q16;
            {var subQ0=sQuery(id+"F0.wireOp",EDGE,"E13");Q16=makeQuery(id+"F2.opShell","OFFSET_EDGE",EDGE,{"disambiguationData":[OSD([subQ0]),TDD([makeQuery(id+"F1.opExtrude","CAP_EDGE",EDGE,{"disambiguationData":[OSD([subQ0])],"isStart":false})]),OD(1.0)]});}
            var Q17;
            {var subQ0=sQuery(id+"F0.wireOp",EDGE,"E7");Q17=makeQuery(id+"F2.opShell","OFFSET_EDGE",EDGE,{"disambiguationData":[OSD([subQ0]),TDD([makeQuery(id+"F1.opExtrude","CAP_EDGE",EDGE,{"disambiguationData":[OSD([subQ0])],"isStart":false})]),OD(1.0)]});}
            var Q18;
            {var subQ0=sQuery(id+"F0.wireOp",EDGE,"E19");Q18=makeQuery(id+"F2.opShell","OFFSET_EDGE",EDGE,{"disambiguationData":[OSD([subQ0]),TDD([makeQuery(id+"F1.opExtrude","CAP_EDGE",EDGE,{"disambiguationData":[OSD([subQ0])],"isStart":true})])]});}
            var Q19;
            {var subQ0=sQuery(id+"F0.wireOp",EDGE,"E13");Q19=makeQuery(id+"F2.opShell","OFFSET_EDGE",EDGE,{"disambiguationData":[OSD([subQ0]),TDD([makeQuery(id+"F1.opExtrude","CAP_EDGE",EDGE,{"disambiguationData":[OSD([subQ0])],"isStart":true})]),OD(0.0)]});}
            var Q20;
            {var subQ0=sQuery(id+"F0.wireOp",EDGE,"E7");Q20=makeQuery(id+"F2.opShell","OFFSET_EDGE",EDGE,{"disambiguationData":[OSD([subQ0]),TDD([makeQuery(id+"F1.opExtrude","CAP_EDGE",EDGE,{"disambiguationData":[OSD([subQ0])],"isStart":true})]),OD(0.0)]});}
            var Q21;
            {var subQ0=sQuery(id+"F0.wireOp",EDGE,"E7");Q21=makeQuery(id+"F2.opShell","OFFSET_EDGE",EDGE,{"disambiguationData":[OSD([subQ0]),TDD([makeQuery(id+"F1.opExtrude","CAP_EDGE",EDGE,{"disambiguationData":[OSD([subQ0])],"isStart":true})]),OD(1.0)]});}
            var Q22;
            {var subQ0=sQuery(id+"F0.wireOp",EDGE,"E22");Q22=makeQuery(id+"F2.opShell","OFFSET_EDGE",EDGE,{"disambiguationData":[OSD([subQ0]),TDD([makeQuery(id+"F1.opExtrude","CAP_EDGE",EDGE,{"disambiguationData":[OSD([subQ0])],"isStart":true})])]});}
            var Q23;
            {var subQ0=sQuery(id+"F0.wireOp",EDGE,"E0");Q23=makeQuery(id+"F2.opShell","OFFSET_EDGE",EDGE,{"disambiguationData":[OSD([subQ0]),TDD([makeQuery(id+"F1.opExtrude","CAP_EDGE",EDGE,{"disambiguationData":[OSD([subQ0])],"isStart":true})]),OD(2.0)]});}
            var Q24;
            {var subQ0=sQuery(id+"F0.wireOp",EDGE,"E9");Q24=makeQuery(id+"F2.opShell","OFFSET_EDGE",EDGE,{"disambiguationData":[OSD([subQ0]),TDD([makeQuery(id+"F1.opExtrude","CAP_EDGE",EDGE,{"disambiguationData":[OSD([subQ0])],"isStart":true})]),OD(0.0)]});}
            var Q25;
            {var subQ0=sQuery(id+"F0.wireOp",EDGE,"E11");Q25=makeQuery(id+"F2.opShell","OFFSET_EDGE",EDGE,{"disambiguationData":[OSD([subQ0]),TDD([makeQuery(id+"F1.opExtrude","CAP_EDGE",EDGE,{"disambiguationData":[OSD([subQ0])],"isStart":true})]),OD(1.0)]});}
            var Q26;
            {var subQ0=sQuery(id+"F0.wireOp",EDGE,"E0");Q26=makeQuery(id+"F2.opShell","OFFSET_EDGE",EDGE,{"disambiguationData":[OSD([subQ0]),TDD([makeQuery(id+"F1.opExtrude","CAP_EDGE",EDGE,{"disambiguationData":[OSD([subQ0])],"isStart":true})]),OD(3.0)]});}
            var Q27;
            {var subQ0=sQuery(id+"F0.wireOp",EDGE,"E13");Q27=makeQuery(id+"F2.opShell","OFFSET_EDGE",EDGE,{"disambiguationData":[OSD([subQ0]),TDD([makeQuery(id+"F1.opExtrude","CAP_EDGE",EDGE,{"disambiguationData":[OSD([subQ0])],"isStart":true})]),OD(1.0)]});}
            var Q28;
            {var subQ0=sQuery(id+"F0.wireOp",EDGE,"E20");Q28=makeQuery(id+"F2.opShell","OFFSET_EDGE",EDGE,{"disambiguationData":[OSD([subQ0]),TDD([makeQuery(id+"F1.opExtrude","CAP_EDGE",EDGE,{"disambiguationData":[OSD([subQ0])],"isStart":true})])]});}
            var Q29;
            {var subQ0=sQuery(id+"F0.wireOp",EDGE,"E11");Q29=makeQuery(id+"F2.opShell","OFFSET_EDGE",EDGE,{"disambiguationData":[OSD([subQ0]),TDD([makeQuery(id+"F1.opExtrude","CAP_EDGE",EDGE,{"disambiguationData":[OSD([subQ0])],"isStart":true})]),OD(0.0)]});}
            var Q30;
            {var subQ0=sQuery(id+"F0.wireOp",EDGE,"E9");Q30=makeQuery(id+"F2.opShell","OFFSET_EDGE",EDGE,{"disambiguationData":[OSD([subQ0]),TDD([makeQuery(id+"F1.opExtrude","CAP_EDGE",EDGE,{"disambiguationData":[OSD([subQ0])],"isStart":true})]),OD(1.0)]});}
            var Q31;
            {var subQ0=sQuery(id+"F0.wireOp",EDGE,"E21");Q31=makeQuery(id+"F2.opShell","OFFSET_EDGE",EDGE,{"disambiguationData":[OSD([subQ0]),TDD([makeQuery(id+"F1.opExtrude","CAP_EDGE",EDGE,{"disambiguationData":[OSD([subQ0])],"isStart":true})])]});}
            chamfer(context, id + "F4", {"entities" : qUnion([Q0, Q1, Q2, Q3, Q4, Q5, Q6, Q7, Q8, Q9, Q10, Q11, Q12, Q13, Q14, Q15, Q16, Q17, Q18, Q19, Q20, Q21, Q22, Q23, Q24, Q25, Q26, Q27, Q28, Q29, Q30, Q31]), "width" : 0.5 * mm, "tangentPropagation" : true});
        }
    });
